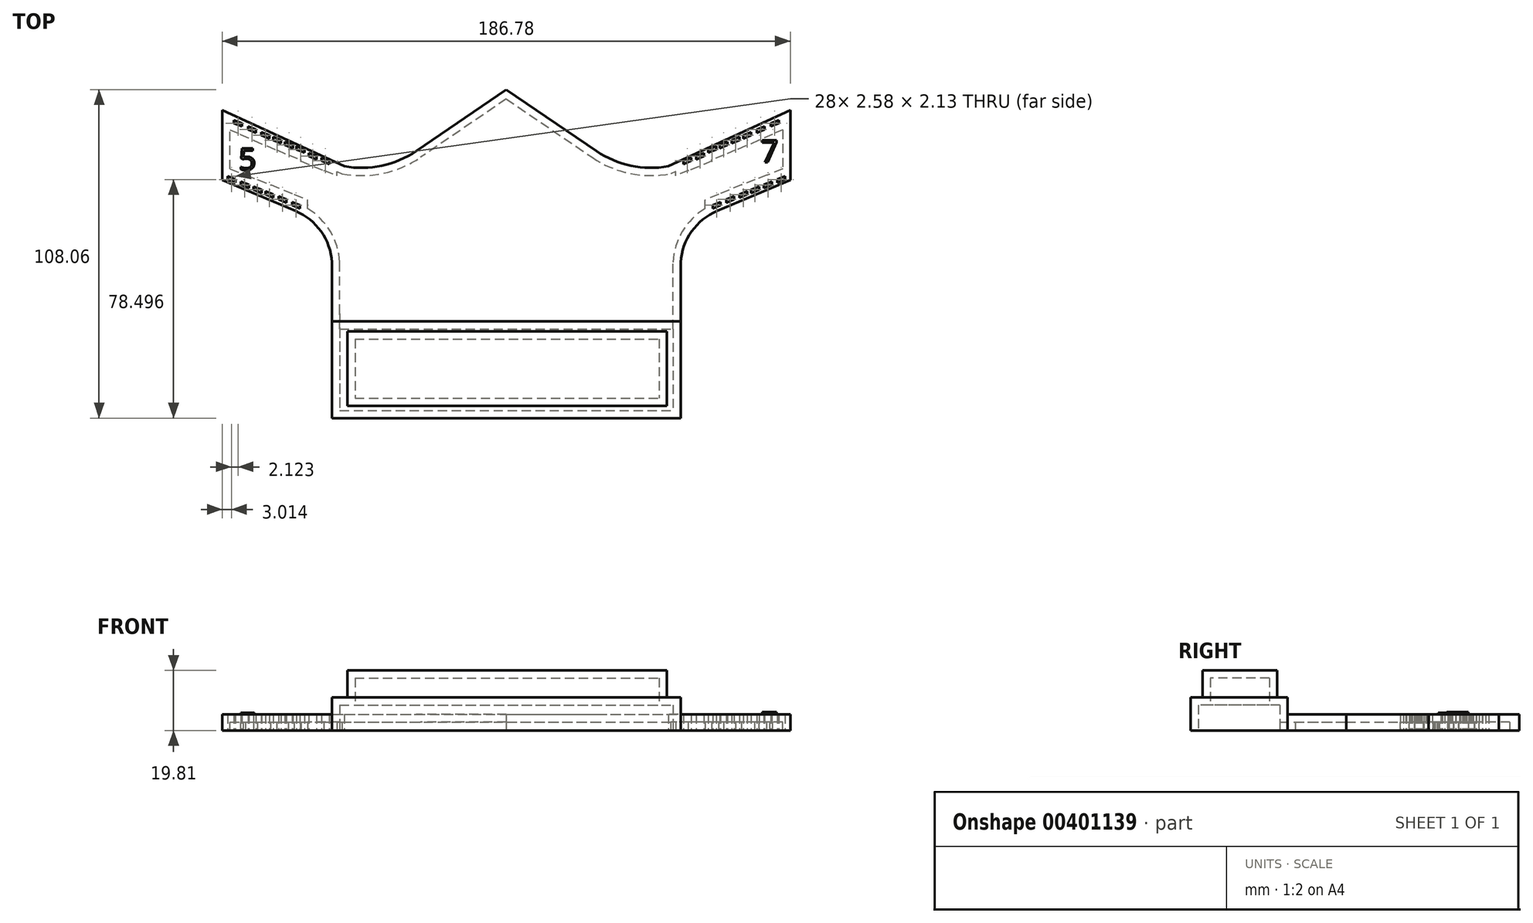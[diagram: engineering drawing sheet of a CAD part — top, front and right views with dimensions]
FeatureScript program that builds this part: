
annotation { "Feature Type Name" : "Feature", "Feature Type Description" : "" }
export const myFeature = defineFeature(function(context is Context, id is Id, definition is map)
    precondition{}
    {
        {
            var Q0;
            Q0=qCreatedBy(makeId("Top.planeOp"),FACE);
            var sketch = newSketch(context, id + "F0", { "sketchPlane" : qUnion([Q0])});
            skLineSegment(sketch, "E0", {"start": v(0, 76.18) * mm, "end": v(-29.66, 55.96) * mm});
            skLineSegment(sketch, "E1", {"start": v(-93.4, 69.44) * mm, "end": v(-53.26, 50.94) * mm});
            skArc(sketch, "E2", {"start": v(-53.26, 50.94) * mm, "mid": v(-40.97, 51.13) * mm, "end": v(-29.66, 55.96) * mm});
            skLineSegment(sketch, "E3", {"start": v(-93.4, 46.4) * mm, "end": v(-69.34, 36.27) * mm});
            skLineSegment(sketch, "E4", {"start": v(-57.32, 0) * mm, "end": v(0, 0) * mm});
            skLineSegment(sketch, "E5", {"start": v(-57.32, 0) * mm, "end": v(-57.32, 19.33) * mm});
            skArc(sketch, "E6", {"start": v(-57.32, 19.33) * mm, "mid": v(-60.91, 29.5) * mm, "end": v(-69.34, 36.27) * mm});
            skLineSegment(sketch, "E7.MirrorCS", {"start": v(0, 76.18) * mm, "end": v(29.66, 55.96) * mm});
            skArc(sketch, "E8.MirrorCS", {"start": v(53.26, 50.94) * mm, "mid": v(40.97, 51.13) * mm, "end": v(29.66, 55.96) * mm});
            skLineSegment(sketch, "E9.MirrorCS", {"start": v(93.4, 69.44) * mm, "end": v(53.26, 50.94) * mm});
            skLineSegment(sketch, "E10.MirrorCS", {"start": v(93.4, 69.44) * mm, "end": v(93.4, 46.4) * mm});
            skLineSegment(sketch, "E11.MirrorCS", {"start": v(93.4, 46.4) * mm, "end": v(69.34, 36.27) * mm});
            skArc(sketch, "E12.MirrorCS", {"start": v(57.32, 19.33) * mm, "mid": v(60.91, 29.5) * mm, "end": v(69.34, 36.27) * mm});
            skLineSegment(sketch, "E13.MirrorCS", {"start": v(57.32, 0) * mm, "end": v(57.32, 19.33) * mm});
            skLineSegment(sketch, "E14.MirrorCS", {"start": v(57.32, 0) * mm, "end": v(0, 0) * mm});
            skLineSegment(sketch, "E15", {"start": v(-152.69, 79.05) * mm, "end": v(-150.33, 88.63) * mm});
            skLineSegment(sketch, "E16", {"start": v(-93.4, 46.4) * mm, "end": v(-93.4, 69.44) * mm});
            skLineSegment(sketch, "E17", {"start": v(-91.66, 46.64) * mm, "end": v(-89.09, 45.55) * mm});
            skLineSegment(sketch, "E18", {"start": v(-91.66, 46.64) * mm, "end": v(-91.66, 47.68) * mm});
            skLineSegment(sketch, "E19", {"start": v(-89.09, 45.55) * mm, "end": v(-89.09, 46.64) * mm});
            skLineSegment(sketch, "E20", {"start": v(-91.66, 47.68) * mm, "end": v(-89.09, 46.64) * mm});
            skLineSegment(sketch, "E21", {"start": v(-87.28, 44.86) * mm, "end": v(-84.7, 43.77) * mm});
            skLineSegment(sketch, "E22", {"start": v(-87.28, 44.86) * mm, "end": v(-87.28, 45.9) * mm});
            skLineSegment(sketch, "E23", {"start": v(-84.7, 43.77) * mm, "end": v(-84.7, 44.86) * mm});
            skLineSegment(sketch, "E24", {"start": v(-87.28, 45.9) * mm, "end": v(-84.7, 44.86) * mm});
            skLineSegment(sketch, "E25", {"start": v(-83.07, 43.23) * mm, "end": v(-80.5, 42.14) * mm});
            skLineSegment(sketch, "E26", {"start": v(-83.07, 43.23) * mm, "end": v(-83.07, 44.27) * mm});
            skLineSegment(sketch, "E27", {"start": v(-80.5, 42.14) * mm, "end": v(-80.5, 43.23) * mm});
            skLineSegment(sketch, "E28", {"start": v(-83.07, 44.27) * mm, "end": v(-80.5, 43.23) * mm});
            skLineSegment(sketch, "E29", {"start": v(-79.22, 41.68) * mm, "end": v(-76.64, 40.6) * mm});
            skLineSegment(sketch, "E30", {"start": v(-79.22, 41.68) * mm, "end": v(-79.22, 42.73) * mm});
            skLineSegment(sketch, "E31", {"start": v(-76.64, 40.6) * mm, "end": v(-76.64, 41.68) * mm});
            skLineSegment(sketch, "E32", {"start": v(-79.22, 42.73) * mm, "end": v(-76.64, 41.68) * mm});
            skLineSegment(sketch, "E33", {"start": v(-74.91, 40.04) * mm, "end": v(-72.33, 38.96) * mm});
            skLineSegment(sketch, "E34", {"start": v(-74.91, 40.04) * mm, "end": v(-74.91, 41.09) * mm});
            skLineSegment(sketch, "E35", {"start": v(-72.33, 38.96) * mm, "end": v(-72.33, 40.04) * mm});
            skLineSegment(sketch, "E36", {"start": v(-74.91, 41.09) * mm, "end": v(-72.33, 40.04) * mm});
            skLineSegment(sketch, "E37", {"start": v(-70.44, 38.16) * mm, "end": v(-67.86, 37.08) * mm});
            skLineSegment(sketch, "E38", {"start": v(-70.44, 38.16) * mm, "end": v(-70.44, 39.2) * mm});
            skLineSegment(sketch, "E39", {"start": v(-67.86, 37.08) * mm, "end": v(-67.86, 38.16) * mm});
            skLineSegment(sketch, "E40", {"start": v(-70.44, 39.2) * mm, "end": v(-67.86, 38.16) * mm});
            skLineSegment(sketch, "E41", {"start": v(-89.54, 65.12) * mm, "end": v(-86.96, 64.04) * mm});
            skLineSegment(sketch, "E42", {"start": v(-89.54, 65.12) * mm, "end": v(-89.54, 66.17) * mm});
            skLineSegment(sketch, "E43", {"start": v(-86.96, 64.04) * mm, "end": v(-86.96, 65.12) * mm});
            skLineSegment(sketch, "E44", {"start": v(-89.54, 66.17) * mm, "end": v(-86.96, 65.12) * mm});
            skLineSegment(sketch, "E45", {"start": v(-84.95, 63.07) * mm, "end": v(-82.37, 61.98) * mm});
            skLineSegment(sketch, "E46", {"start": v(-84.95, 63.07) * mm, "end": v(-84.95, 64.1) * mm});
            skLineSegment(sketch, "E47", {"start": v(-82.37, 61.98) * mm, "end": v(-82.37, 63.07) * mm});
            skLineSegment(sketch, "E48", {"start": v(-84.95, 64.1) * mm, "end": v(-82.37, 63.07) * mm});
            skLineSegment(sketch, "E49", {"start": v(-80.52, 61.14) * mm, "end": v(-77.94, 60.06) * mm});
            skLineSegment(sketch, "E50", {"start": v(-80.52, 61.14) * mm, "end": v(-80.52, 62.19) * mm});
            skLineSegment(sketch, "E51", {"start": v(-77.94, 60.06) * mm, "end": v(-77.94, 61.14) * mm});
            skLineSegment(sketch, "E52", {"start": v(-80.52, 62.19) * mm, "end": v(-77.94, 61.14) * mm});
            skLineSegment(sketch, "E53", {"start": v(-76.64, 59.56) * mm, "end": v(-74.06, 58.48) * mm});
            skLineSegment(sketch, "E54", {"start": v(-76.64, 59.56) * mm, "end": v(-76.64, 60.6) * mm});
            skLineSegment(sketch, "E55", {"start": v(-74.06, 58.48) * mm, "end": v(-74.06, 59.56) * mm});
            skLineSegment(sketch, "E56", {"start": v(-76.64, 60.6) * mm, "end": v(-74.06, 59.56) * mm});
            skLineSegment(sketch, "E57", {"start": v(-72.77, 57.97) * mm, "end": v(-70.2, 56.89) * mm});
            skLineSegment(sketch, "E58", {"start": v(-72.77, 57.97) * mm, "end": v(-72.77, 59.01) * mm});
            skLineSegment(sketch, "E59", {"start": v(-70.2, 56.89) * mm, "end": v(-70.2, 57.97) * mm});
            skLineSegment(sketch, "E60", {"start": v(-72.77, 59.01) * mm, "end": v(-70.2, 57.97) * mm});
            skLineSegment(sketch, "E61", {"start": v(-68.97, 56.51) * mm, "end": v(-66.39, 55.43) * mm});
            skLineSegment(sketch, "E62", {"start": v(-68.97, 56.51) * mm, "end": v(-68.97, 57.56) * mm});
            skLineSegment(sketch, "E63", {"start": v(-66.39, 55.43) * mm, "end": v(-66.39, 56.51) * mm});
            skLineSegment(sketch, "E64", {"start": v(-68.97, 57.56) * mm, "end": v(-66.39, 56.51) * mm});
            skLineSegment(sketch, "E65", {"start": v(-65.01, 54.3) * mm, "end": v(-62.44, 53.21) * mm});
            skLineSegment(sketch, "E66", {"start": v(-65.01, 54.3) * mm, "end": v(-65.01, 55.34) * mm});
            skLineSegment(sketch, "E67", {"start": v(-62.44, 53.21) * mm, "end": v(-62.44, 54.3) * mm});
            skLineSegment(sketch, "E68", {"start": v(-65.01, 55.34) * mm, "end": v(-62.44, 54.3) * mm});
            skLineSegment(sketch, "E69", {"start": v(-60.83, 52.75) * mm, "end": v(-58.25, 51.66) * mm});
            skLineSegment(sketch, "E70", {"start": v(-60.83, 52.75) * mm, "end": v(-60.83, 53.8) * mm});
            skLineSegment(sketch, "E71", {"start": v(-58.25, 51.66) * mm, "end": v(-58.25, 52.75) * mm});
            skLineSegment(sketch, "E72", {"start": v(-60.83, 53.8) * mm, "end": v(-58.25, 52.75) * mm});
            skLineSegment(sketch, "E73.MirrorCS", {"start": v(89.54, 65.12) * mm, "end": v(86.96, 64.04) * mm});
            skLineSegment(sketch, "E74.MirrorCS", {"start": v(89.54, 66.17) * mm, "end": v(86.96, 65.12) * mm});
            skLineSegment(sketch, "E75.MirrorCS", {"start": v(89.54, 65.12) * mm, "end": v(89.54, 66.17) * mm});
            skLineSegment(sketch, "E76.MirrorCS", {"start": v(86.96, 64.04) * mm, "end": v(86.96, 65.12) * mm});
            skLineSegment(sketch, "E77.MirrorCS", {"start": v(84.95, 63.07) * mm, "end": v(84.95, 64.1) * mm});
            skLineSegment(sketch, "E78.MirrorCS", {"start": v(84.95, 64.1) * mm, "end": v(82.37, 63.07) * mm});
            skLineSegment(sketch, "E79.MirrorCS", {"start": v(84.95, 63.07) * mm, "end": v(82.37, 61.98) * mm});
            skLineSegment(sketch, "E80.MirrorCS", {"start": v(82.37, 61.98) * mm, "end": v(82.37, 63.07) * mm});
            skLineSegment(sketch, "E81.MirrorCS", {"start": v(80.52, 61.14) * mm, "end": v(80.52, 62.19) * mm});
            skLineSegment(sketch, "E82.MirrorCS", {"start": v(80.52, 62.19) * mm, "end": v(77.94, 61.14) * mm});
            skLineSegment(sketch, "E83.MirrorCS", {"start": v(80.52, 61.14) * mm, "end": v(77.94, 60.06) * mm});
            skLineSegment(sketch, "E84.MirrorCS", {"start": v(77.94, 60.06) * mm, "end": v(77.94, 61.14) * mm});
            skLineSegment(sketch, "E85.MirrorCS", {"start": v(76.64, 59.56) * mm, "end": v(76.64, 60.6) * mm});
            skLineSegment(sketch, "E86.MirrorCS", {"start": v(74.06, 58.48) * mm, "end": v(74.06, 59.56) * mm});
            skLineSegment(sketch, "E87.MirrorCS", {"start": v(76.64, 60.6) * mm, "end": v(74.06, 59.56) * mm});
            skLineSegment(sketch, "E88.MirrorCS", {"start": v(76.64, 59.56) * mm, "end": v(74.06, 58.48) * mm});
            skLineSegment(sketch, "E89.MirrorCS", {"start": v(72.77, 57.97) * mm, "end": v(70.2, 56.89) * mm});
            skLineSegment(sketch, "E90.MirrorCS", {"start": v(72.77, 59.01) * mm, "end": v(70.2, 57.97) * mm});
            skLineSegment(sketch, "E91.MirrorCS", {"start": v(72.77, 57.97) * mm, "end": v(72.77, 59.01) * mm});
            skLineSegment(sketch, "E92.MirrorCS", {"start": v(70.2, 56.89) * mm, "end": v(70.2, 57.97) * mm});
            skLineSegment(sketch, "E93.MirrorCS", {"start": v(68.97, 56.51) * mm, "end": v(68.97, 57.56) * mm});
            skLineSegment(sketch, "E94.MirrorCS", {"start": v(68.97, 57.56) * mm, "end": v(66.39, 56.51) * mm});
            skLineSegment(sketch, "E95.MirrorCS", {"start": v(68.97, 56.51) * mm, "end": v(66.39, 55.43) * mm});
            skLineSegment(sketch, "E96.MirrorCS", {"start": v(66.39, 55.43) * mm, "end": v(66.39, 56.51) * mm});
            skLineSegment(sketch, "E97.MirrorCS", {"start": v(65.01, 55.34) * mm, "end": v(62.44, 54.3) * mm});
            skLineSegment(sketch, "E98.MirrorCS", {"start": v(65.01, 54.3) * mm, "end": v(62.44, 53.21) * mm});
            skLineSegment(sketch, "E99.MirrorCS", {"start": v(65.01, 54.3) * mm, "end": v(65.01, 55.34) * mm});
            skLineSegment(sketch, "E100.MirrorCS", {"start": v(62.44, 53.21) * mm, "end": v(62.44, 54.3) * mm});
            skLineSegment(sketch, "E101.MirrorCS", {"start": v(60.83, 52.75) * mm, "end": v(60.83, 53.8) * mm});
            skLineSegment(sketch, "E102.MirrorCS", {"start": v(58.25, 51.66) * mm, "end": v(58.25, 52.75) * mm});
            skLineSegment(sketch, "E103.MirrorCS", {"start": v(60.83, 53.8) * mm, "end": v(58.25, 52.75) * mm});
            skLineSegment(sketch, "E104.MirrorCS", {"start": v(60.83, 52.75) * mm, "end": v(58.25, 51.66) * mm});
            skLineSegment(sketch, "E105.MirrorCS", {"start": v(91.66, 47.68) * mm, "end": v(89.09, 46.64) * mm});
            skLineSegment(sketch, "E106.MirrorCS", {"start": v(87.28, 45.9) * mm, "end": v(84.7, 44.86) * mm});
            skLineSegment(sketch, "E107.MirrorCS", {"start": v(83.07, 44.27) * mm, "end": v(80.5, 43.23) * mm});
            skLineSegment(sketch, "E108.MirrorCS", {"start": v(79.22, 42.73) * mm, "end": v(76.64, 41.68) * mm});
            skLineSegment(sketch, "E109.MirrorCS", {"start": v(74.91, 41.09) * mm, "end": v(72.33, 40.04) * mm});
            skLineSegment(sketch, "E110.MirrorCS", {"start": v(70.44, 39.2) * mm, "end": v(67.86, 38.16) * mm});
            skLineSegment(sketch, "E111.MirrorCS", {"start": v(91.66, 46.64) * mm, "end": v(91.66, 47.68) * mm});
            skLineSegment(sketch, "E112.MirrorCS", {"start": v(89.09, 45.55) * mm, "end": v(89.09, 46.64) * mm});
            skLineSegment(sketch, "E113.MirrorCS", {"start": v(87.28, 44.86) * mm, "end": v(87.28, 45.9) * mm});
            skLineSegment(sketch, "E114.MirrorCS", {"start": v(84.7, 43.77) * mm, "end": v(84.7, 44.86) * mm});
            skLineSegment(sketch, "E115.MirrorCS", {"start": v(83.07, 43.23) * mm, "end": v(83.07, 44.27) * mm});
            skLineSegment(sketch, "E116.MirrorCS", {"start": v(80.5, 42.14) * mm, "end": v(80.5, 43.23) * mm});
            skLineSegment(sketch, "E117.MirrorCS", {"start": v(79.22, 41.68) * mm, "end": v(79.22, 42.73) * mm});
            skLineSegment(sketch, "E118.MirrorCS", {"start": v(76.64, 40.6) * mm, "end": v(76.64, 41.68) * mm});
            skLineSegment(sketch, "E119.MirrorCS", {"start": v(74.91, 40.04) * mm, "end": v(74.91, 41.09) * mm});
            skLineSegment(sketch, "E120.MirrorCS", {"start": v(72.33, 38.96) * mm, "end": v(72.33, 40.04) * mm});
            skLineSegment(sketch, "E121.MirrorCS", {"start": v(70.44, 38.16) * mm, "end": v(70.44, 39.2) * mm});
            skLineSegment(sketch, "E122.MirrorCS", {"start": v(67.86, 37.08) * mm, "end": v(67.86, 38.16) * mm});
            skLineSegment(sketch, "E123.MirrorCS", {"start": v(70.44, 38.16) * mm, "end": v(67.86, 37.08) * mm});
            skLineSegment(sketch, "E124.MirrorCS", {"start": v(74.91, 40.04) * mm, "end": v(72.33, 38.96) * mm});
            skLineSegment(sketch, "E125.MirrorCS", {"start": v(79.22, 41.68) * mm, "end": v(76.64, 40.6) * mm});
            skLineSegment(sketch, "E126.MirrorCS", {"start": v(83.07, 43.23) * mm, "end": v(80.5, 42.14) * mm});
            skLineSegment(sketch, "E127.MirrorCS", {"start": v(87.28, 44.86) * mm, "end": v(84.7, 43.77) * mm});
            skLineSegment(sketch, "E128.MirrorCS", {"start": v(91.66, 46.64) * mm, "end": v(89.09, 45.55) * mm});
            skSolve(sketch);
        }
        {
            var Q0;
            Q0=makeQuery(id+"F0.imprint","IMPRINT",FACE,{"disambiguationData":[TD([[makeQuery(id+"F0.imprint","IMPRINT",EDGE,{"derivedFrom":sQuery(id+"F0.wireOp",EDGE,"E0")}),1.0]])]});
            extrude(context, id + "F1", {"entities" : qUnion([Q0]), "depth" : 5.33 * mm});
        }
        {
            var Q0;
            Q0=qCreatedBy(makeId("Top.planeOp"),FACE);
            var sketch = newSketch(context, id + "F2", { "sketchPlane" : qUnion([Q0])});
            skLineSegment(sketch, "E129.bottom", {"start": v(-57.3, 0) * mm, "end": v(57.38, 0) * mm});
            skLineSegment(sketch, "E129.top", {"start": v(-57.3, -31.88) * mm, "end": v(57.38, -31.88) * mm});
            skLineSegment(sketch, "E129.left", {"start": v(-57.3, 0) * mm, "end": v(-57.3, -31.88) * mm});
            skLineSegment(sketch, "E129.right", {"start": v(57.38, 0) * mm, "end": v(57.38, -31.88) * mm});
            skSolve(sketch);
        }
        {
            var Q0;
            Q0 = qSketchRegion(id + "F2", true);
            extrude(context, id + "F3", {"entities" : qUnion([Q0]), "operationType" : NewBodyOperationType.ADD, "depth" : 10.92 * mm});
        }
        {
            var Q0;
            Q0=makeQuery(id+"F3.opExtrude","CAP_FACE",FACE,{"disambiguationData":[OSD([sQuery(id+"F2.wireOp",EDGE,"E129.bottom"),sQuery(id+"F2.wireOp",EDGE,"E129.top"),sQuery(id+"F2.wireOp",EDGE,"E129.left"),sQuery(id+"F2.wireOp",EDGE,"E129.right")])],"isStart":false});
            var sketch = newSketch(context, id + "F4", { "sketchPlane" : qUnion([Q0])});
            skLineSegment(sketch, "E130.bottom", {"start": v(-52.27, -3.39) * mm, "end": v(52.77, -3.39) * mm});
            skLineSegment(sketch, "E130.top", {"start": v(-52.27, -27.85) * mm, "end": v(52.77, -27.85) * mm});
            skLineSegment(sketch, "E130.left", {"start": v(-52.27, -3.39) * mm, "end": v(-52.27, -27.85) * mm});
            skLineSegment(sketch, "E130.right", {"start": v(52.77, -3.39) * mm, "end": v(52.77, -27.85) * mm});
            skSolve(sketch);
        }
        {
            var Q0;
            Q0 = qSketchRegion(id + "F4", true);
            extrude(context, id + "F5", {"entities" : qUnion([Q0]), "operationType" : NewBodyOperationType.ADD, "depth" : 8.9 * mm});
        }
        {
            var Q0;
            Q0=makeQuery(id+"F3.boolean.opBoolean","MERGE",FACE,{"derivedFrom":[makeQuery(id+"F1.opExtrude","CAP_FACE",FACE,{"disambiguationData":[OSD([sQuery(id+"F0.wireOp",EDGE,"E0"),sQuery(id+"F0.wireOp",EDGE,"E1"),sQuery(id+"F0.wireOp",EDGE,"E2"),sQuery(id+"F0.wireOp",EDGE,"vuTD4XOv-XI36-b5Hq-LpK4-bp7VUpcFpueW"),sQuery(id+"F0.wireOp",EDGE,"E3"),sQuery(id+"F0.wireOp",EDGE,"E4"),sQuery(id+"F0.wireOp",EDGE,"E5"),sQuery(id+"F0.wireOp",EDGE,"E6"),sQuery(id+"F0.wireOp",EDGE,"E7.MirrorCS"),sQuery(id+"F0.wireOp",EDGE,"E8.MirrorCS"),sQuery(id+"F0.wireOp",EDGE,"E9.MirrorCS"),sQuery(id+"F0.wireOp",EDGE,"E10.MirrorCS"),sQuery(id+"F0.wireOp",EDGE,"E11.MirrorCS"),sQuery(id+"F0.wireOp",EDGE,"E12.MirrorCS"),sQuery(id+"F0.wireOp",EDGE,"E13.MirrorCS"),sQuery(id+"F0.wireOp",EDGE,"E14.MirrorCS")])],"isStart":true}),makeQuery(id+"F3.opExtrude","CAP_FACE",FACE,{"disambiguationData":[OSD([sQuery(id+"F2.wireOp",EDGE,"E129.bottom"),sQuery(id+"F2.wireOp",EDGE,"E129.top"),sQuery(id+"F2.wireOp",EDGE,"E129.left"),sQuery(id+"F2.wireOp",EDGE,"E129.right")])],"isStart":true})]});
            shell(context, id + "F6", {"entities" : qUnion([Q0]), "thickness" : 2.54 * mm});
        }
        {
            var Q0;
            Q0=makeQuery(id+"F1.opExtrude","CAP_FACE",FACE,{"disambiguationData":[OSD([sQuery(id+"F0.wireOp",EDGE,"E0"),sQuery(id+"F0.wireOp",EDGE,"E1"),sQuery(id+"F0.wireOp",EDGE,"E2"),sQuery(id+"F0.wireOp",EDGE,"E3"),sQuery(id+"F0.wireOp",EDGE,"E4"),sQuery(id+"F0.wireOp",EDGE,"E5"),sQuery(id+"F0.wireOp",EDGE,"E6"),sQuery(id+"F0.wireOp",EDGE,"E7.MirrorCS"),sQuery(id+"F0.wireOp",EDGE,"E8.MirrorCS"),sQuery(id+"F0.wireOp",EDGE,"E9.MirrorCS"),sQuery(id+"F0.wireOp",EDGE,"E10.MirrorCS"),sQuery(id+"F0.wireOp",EDGE,"E11.MirrorCS"),sQuery(id+"F0.wireOp",EDGE,"E12.MirrorCS"),sQuery(id+"F0.wireOp",EDGE,"E13.MirrorCS"),sQuery(id+"F0.wireOp",EDGE,"E14.MirrorCS"),sQuery(id+"F0.wireOp",EDGE,"E16"),sQuery(id+"F0.wireOp",EDGE,"E17"),sQuery(id+"F0.wireOp",EDGE,"E18"),sQuery(id+"F0.wireOp",EDGE,"E19"),sQuery(id+"F0.wireOp",EDGE,"E20"),sQuery(id+"F0.wireOp",EDGE,"E21"),sQuery(id+"F0.wireOp",EDGE,"E22"),sQuery(id+"F0.wireOp",EDGE,"E23"),sQuery(id+"F0.wireOp",EDGE,"E24"),sQuery(id+"F0.wireOp",EDGE,"E25"),sQuery(id+"F0.wireOp",EDGE,"E26"),sQuery(id+"F0.wireOp",EDGE,"E27"),sQuery(id+"F0.wireOp",EDGE,"E28"),sQuery(id+"F0.wireOp",EDGE,"E29"),sQuery(id+"F0.wireOp",EDGE,"E30"),sQuery(id+"F0.wireOp",EDGE,"E31"),sQuery(id+"F0.wireOp",EDGE,"E32"),sQuery(id+"F0.wireOp",EDGE,"E33"),sQuery(id+"F0.wireOp",EDGE,"E34"),sQuery(id+"F0.wireOp",EDGE,"E35"),sQuery(id+"F0.wireOp",EDGE,"E36"),sQuery(id+"F0.wireOp",EDGE,"E37"),sQuery(id+"F0.wireOp",EDGE,"E38"),sQuery(id+"F0.wireOp",EDGE,"E39"),sQuery(id+"F0.wireOp",EDGE,"E40"),sQuery(id+"F0.wireOp",EDGE,"E41"),sQuery(id+"F0.wireOp",EDGE,"E42"),sQuery(id+"F0.wireOp",EDGE,"E43"),sQuery(id+"F0.wireOp",EDGE,"E44"),sQuery(id+"F0.wireOp",EDGE,"E45"),sQuery(id+"F0.wireOp",EDGE,"E46"),sQuery(id+"F0.wireOp",EDGE,"E47"),sQuery(id+"F0.wireOp",EDGE,"E48"),sQuery(id+"F0.wireOp",EDGE,"E49"),sQuery(id+"F0.wireOp",EDGE,"E50"),sQuery(id+"F0.wireOp",EDGE,"E51"),sQuery(id+"F0.wireOp",EDGE,"E52"),sQuery(id+"F0.wireOp",EDGE,"E53"),sQuery(id+"F0.wireOp",EDGE,"E54"),sQuery(id+"F0.wireOp",EDGE,"E55"),sQuery(id+"F0.wireOp",EDGE,"E56"),sQuery(id+"F0.wireOp",EDGE,"E57"),sQuery(id+"F0.wireOp",EDGE,"E58"),sQuery(id+"F0.wireOp",EDGE,"E59"),sQuery(id+"F0.wireOp",EDGE,"E60"),sQuery(id+"F0.wireOp",EDGE,"E61"),sQuery(id+"F0.wireOp",EDGE,"E62"),sQuery(id+"F0.wireOp",EDGE,"E63"),sQuery(id+"F0.wireOp",EDGE,"E64"),sQuery(id+"F0.wireOp",EDGE,"E65"),sQuery(id+"F0.wireOp",EDGE,"E66"),sQuery(id+"F0.wireOp",EDGE,"E67"),sQuery(id+"F0.wireOp",EDGE,"E68"),sQuery(id+"F0.wireOp",EDGE,"E69"),sQuery(id+"F0.wireOp",EDGE,"E70"),sQuery(id+"F0.wireOp",EDGE,"E71"),sQuery(id+"F0.wireOp",EDGE,"E72")])],"isStart":false});
            var sketch = newSketch(context, id + "F7", { "sketchPlane" : qUnion([Q0])});
            skText(sketch, "E131", { "text": "5", "fontName": "OpenSans-Regular.ttf"});
            const initialGuessF7  = {"E131": [-0.08802, 0.04972, 1, 0, 0.00722]};
            skSetInitialGuess(sketch, initialGuessF7);
            skSolve(sketch);
        }
        {
            var Q0;
            Q0 = qSketchRegion(id + "F7", true);
            extrude(context, id + "F8", {"entities" : qUnion([Q0]), "operationType" : NewBodyOperationType.ADD, "depth" : 0.5 * mm});
        }
        {
            var Q0;
            Q0=makeQuery(id+"F1.opExtrude","CAP_FACE",FACE,{"disambiguationData":[OSD([sQuery(id+"F0.wireOp",EDGE,"E0"),sQuery(id+"F0.wireOp",EDGE,"E1"),sQuery(id+"F0.wireOp",EDGE,"E2"),sQuery(id+"F0.wireOp",EDGE,"E3"),sQuery(id+"F0.wireOp",EDGE,"E4"),sQuery(id+"F0.wireOp",EDGE,"E5"),sQuery(id+"F0.wireOp",EDGE,"E6"),sQuery(id+"F0.wireOp",EDGE,"E7.MirrorCS"),sQuery(id+"F0.wireOp",EDGE,"E8.MirrorCS"),sQuery(id+"F0.wireOp",EDGE,"E9.MirrorCS"),sQuery(id+"F0.wireOp",EDGE,"E10.MirrorCS"),sQuery(id+"F0.wireOp",EDGE,"E11.MirrorCS"),sQuery(id+"F0.wireOp",EDGE,"E12.MirrorCS"),sQuery(id+"F0.wireOp",EDGE,"E13.MirrorCS"),sQuery(id+"F0.wireOp",EDGE,"E14.MirrorCS"),sQuery(id+"F0.wireOp",EDGE,"E16"),sQuery(id+"F0.wireOp",EDGE,"E17"),sQuery(id+"F0.wireOp",EDGE,"E18"),sQuery(id+"F0.wireOp",EDGE,"E19"),sQuery(id+"F0.wireOp",EDGE,"E20"),sQuery(id+"F0.wireOp",EDGE,"E21"),sQuery(id+"F0.wireOp",EDGE,"E22"),sQuery(id+"F0.wireOp",EDGE,"E23"),sQuery(id+"F0.wireOp",EDGE,"E24"),sQuery(id+"F0.wireOp",EDGE,"E25"),sQuery(id+"F0.wireOp",EDGE,"E26"),sQuery(id+"F0.wireOp",EDGE,"E27"),sQuery(id+"F0.wireOp",EDGE,"E28"),sQuery(id+"F0.wireOp",EDGE,"E29"),sQuery(id+"F0.wireOp",EDGE,"E30"),sQuery(id+"F0.wireOp",EDGE,"E31"),sQuery(id+"F0.wireOp",EDGE,"E32"),sQuery(id+"F0.wireOp",EDGE,"E33"),sQuery(id+"F0.wireOp",EDGE,"E34"),sQuery(id+"F0.wireOp",EDGE,"E35"),sQuery(id+"F0.wireOp",EDGE,"E36"),sQuery(id+"F0.wireOp",EDGE,"E37"),sQuery(id+"F0.wireOp",EDGE,"E38"),sQuery(id+"F0.wireOp",EDGE,"E39"),sQuery(id+"F0.wireOp",EDGE,"E40"),sQuery(id+"F0.wireOp",EDGE,"E41"),sQuery(id+"F0.wireOp",EDGE,"E42"),sQuery(id+"F0.wireOp",EDGE,"E43"),sQuery(id+"F0.wireOp",EDGE,"E44"),sQuery(id+"F0.wireOp",EDGE,"E45"),sQuery(id+"F0.wireOp",EDGE,"E46"),sQuery(id+"F0.wireOp",EDGE,"E47"),sQuery(id+"F0.wireOp",EDGE,"E48"),sQuery(id+"F0.wireOp",EDGE,"E49"),sQuery(id+"F0.wireOp",EDGE,"E50"),sQuery(id+"F0.wireOp",EDGE,"E51"),sQuery(id+"F0.wireOp",EDGE,"E52"),sQuery(id+"F0.wireOp",EDGE,"E53"),sQuery(id+"F0.wireOp",EDGE,"E54"),sQuery(id+"F0.wireOp",EDGE,"E55"),sQuery(id+"F0.wireOp",EDGE,"E56"),sQuery(id+"F0.wireOp",EDGE,"E57"),sQuery(id+"F0.wireOp",EDGE,"E58"),sQuery(id+"F0.wireOp",EDGE,"E59"),sQuery(id+"F0.wireOp",EDGE,"E60"),sQuery(id+"F0.wireOp",EDGE,"E61"),sQuery(id+"F0.wireOp",EDGE,"E62"),sQuery(id+"F0.wireOp",EDGE,"E63"),sQuery(id+"F0.wireOp",EDGE,"E64"),sQuery(id+"F0.wireOp",EDGE,"E65"),sQuery(id+"F0.wireOp",EDGE,"E66"),sQuery(id+"F0.wireOp",EDGE,"E67"),sQuery(id+"F0.wireOp",EDGE,"E68"),sQuery(id+"F0.wireOp",EDGE,"E69"),sQuery(id+"F0.wireOp",EDGE,"E70"),sQuery(id+"F0.wireOp",EDGE,"E71"),sQuery(id+"F0.wireOp",EDGE,"E72")])],"isStart":false});
            var sketch = newSketch(context, id + "F9", { "sketchPlane" : qUnion([Q0])});
            skText(sketch, "E132", { "text": "7\n", "fontName": "OpenSans-Regular.ttf"});
            const initialGuessF9  = {"E132": [0.08367, 0.05231, 1, 0, 0.00722]};
            skSetInitialGuess(sketch, initialGuessF9);
            skSolve(sketch);
        }
        {
            var Q0;
            Q0 = qSketchRegion(id + "F9", true);
            extrude(context, id + "F10", {"entities" : qUnion([Q0]), "operationType" : NewBodyOperationType.ADD, "depth" : 0.76 * mm});
        }
    });
